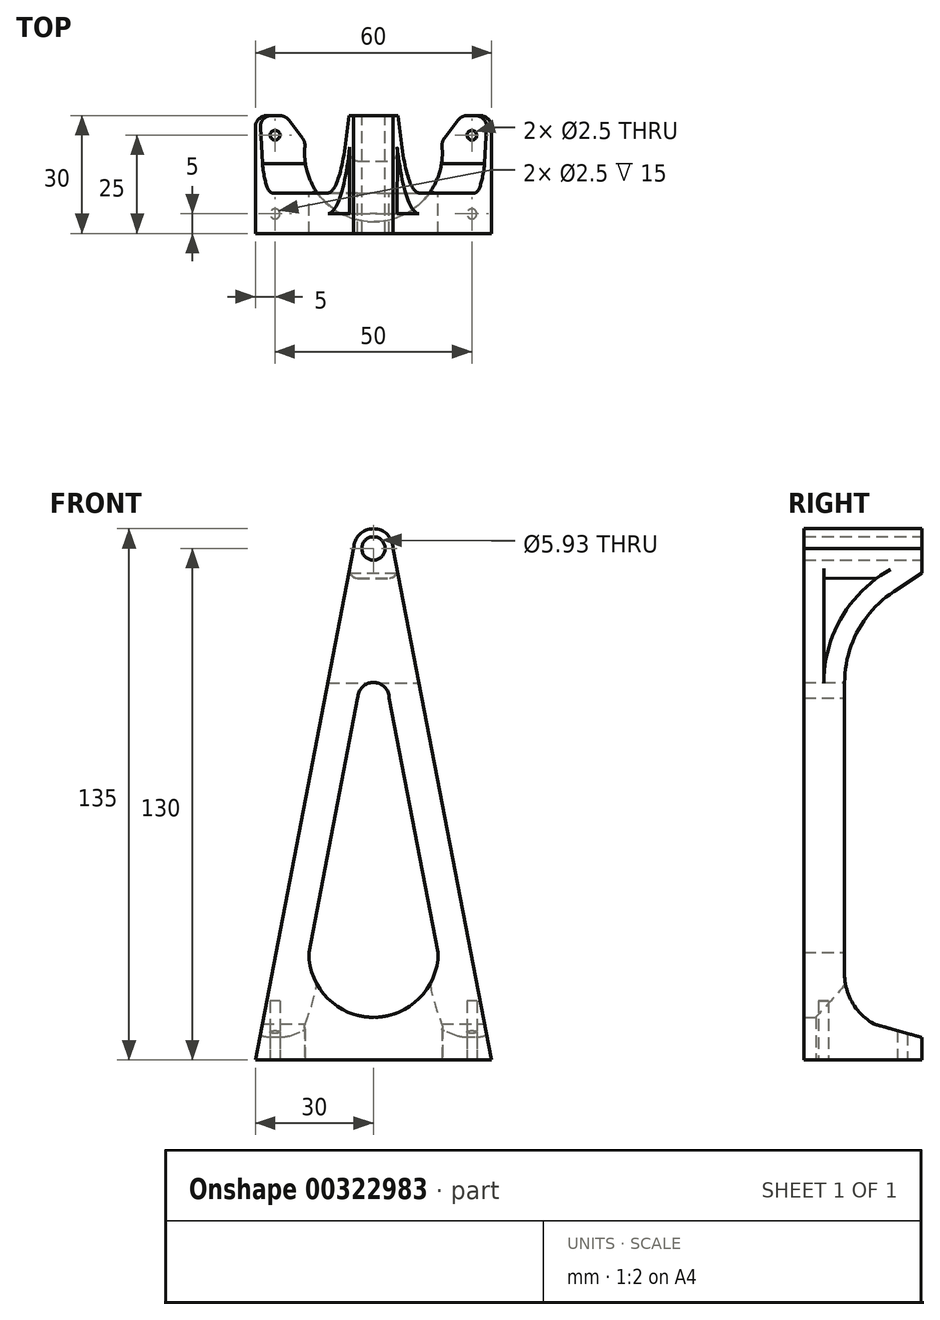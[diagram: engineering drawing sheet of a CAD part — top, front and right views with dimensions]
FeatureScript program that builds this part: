
annotation { "Feature Type Name" : "Feature", "Feature Type Description" : "" }
export const myFeature = defineFeature(function(context is Context, id is Id, definition is map)
    precondition{}
    {
        {
            var Q0;
            Q0=qCreatedBy(makeId("Front.planeOp"),FACE);
            var sketch = newSketch(context, id + "F0", { "sketchPlane" : qUnion([Q0])});
            skLineSegment(sketch, "E0", {"start": v(0, 0) * mm, "end": v(0, 130) * mm, "construction": true});
            skLineSegment(sketch, "E1", {"start": v(0, 130) * mm, "end": v(-5, 130) * mm, "construction": true});
            skLineSegment(sketch, "E2", {"start": v(0, 0) * mm, "end": v(-30, 0) * mm});
            skLineSegment(sketch, "E3", {"start": v(-30, 0) * mm, "end": v(-5, 130) * mm});
            skLineSegment(sketch, "E4.MirrorCS", {"start": v(30, 0) * mm, "end": v(5, 130) * mm});
            skLineSegment(sketch, "E5.MirrorCS", {"start": v(0, 0) * mm, "end": v(30, 0) * mm});
            skArc(sketch, "E6", {"start": v(-5, 130) * mm, "mid": v(0, 135) * mm, "end": v(5, 130) * mm});
            skCircle(sketch, "E7", {"center": v(0, 27.3) * mm, "radius": 16.43 * mm, "construction": true});
            skCircle(sketch, "E8", {"center": v(0, 130) * mm, "radius": 5 * mm, "construction": true});
            skCircle(sketch, "E9", {"center": v(0, 115.44) * mm, "radius": 0.58 * mm, "construction": true});
            skLineSegment(sketch, "E10", {"start": v(-0.31, 115.93) * mm, "end": v(16.13, 30.4) * mm, "construction": true});
            skLineSegment(sketch, "E11.MirrorCS", {"start": v(0.31, 115.93) * mm, "end": v(-16.13, 30.4) * mm, "construction": true});
            skCircle(sketch, "E12", {"center": v(0, 91.94) * mm, "radius": 4.22 * mm, "construction": true});
            skLineSegment(sketch, "E13", {"start": v(0, 91.94) * mm, "end": v(-10.67, 91.94) * mm, "construction": true});
            skLineSegment(sketch, "E14", {"start": v(0, 91.94) * mm, "end": v(7.84, 91.94) * mm, "construction": true});
            skLineSegment(sketch, "E15", {"start": v(0, 27.3) * mm, "end": v(21.13, 27.3) * mm, "construction": true});
            skLineSegment(sketch, "E16", {"start": v(0, 27.3) * mm, "end": v(-22.3, 27.3) * mm, "construction": true});
            skLineSegment(sketch, "E17", {"start": v(-16.43, 27.3) * mm, "end": v(-4, 91.94) * mm});
            skLineSegment(sketch, "E18.MirrorCS", {"start": v(16.43, 27.3) * mm, "end": v(4, 91.94) * mm});
            skArc(sketch, "E19", {"start": v(-4, 91.94) * mm, "mid": v(0, 95.94) * mm, "end": v(4, 91.94) * mm});
            skArc(sketch, "E20", {"start": v(-16.43, 27.3) * mm, "mid": v(0, 10.87) * mm, "end": v(16.43, 27.3) * mm});
            skCircle(sketch, "E21", {"center": v(0, 130) * mm, "radius": 2.97 * mm});
            skSolve(sketch);
        }
        {
            var Q0;
            Q0 = qSketchRegion(id + "F0", true);
            extrude(context, id + "F1", {"entities" : qUnion([Q0]), "depth" : 30 * mm, "symmetric" : true});
        }
        {
            var Q0;
            Q0=qCreatedBy(makeId("Top.planeOp"),FACE);
            var sketch = newSketch(context, id + "F2", { "sketchPlane" : qUnion([Q0])});
            skLineSegment(sketch, "E22.bottom", {"start": v(31.25, -15.95) * mm, "end": v(-31.25, -15.95) * mm, "construction": true});
            skLineSegment(sketch, "E22.top", {"start": v(31.25, 15.95) * mm, "end": v(-31.25, 15.95) * mm, "construction": true});
            skLineSegment(sketch, "E22.left", {"start": v(31.25, -15.95) * mm, "end": v(31.25, 15.95) * mm, "construction": true});
            skLineSegment(sketch, "E22.right", {"start": v(-31.25, -15.95) * mm, "end": v(-31.25, 15.95) * mm, "construction": true});
            skPoint(sketch, "E22.middle", {"position": v(0, 0) * mm});
            skLineSegment(sketch, "E23.bottom", {"start": v(25, -10) * mm, "end": v(-25, -10) * mm, "construction": true});
            skLineSegment(sketch, "E23.top", {"start": v(25, 10) * mm, "end": v(-25, 10) * mm, "construction": true});
            skLineSegment(sketch, "E23.left", {"start": v(25, -10) * mm, "end": v(25, 10) * mm, "construction": true});
            skLineSegment(sketch, "E23.right", {"start": v(-25, -10) * mm, "end": v(-25, 10) * mm, "construction": true});
            skCircle(sketch, "E24", {"center": v(-25, -10) * mm, "radius": 1.25 * mm});
            skLineSegment(sketch, "E25", {"start": v(-25, 10) * mm, "end": v(25, 10) * mm});
            skCircle(sketch, "E26", {"center": v(-25, 10) * mm, "radius": 1.25 * mm});
            skCircle(sketch, "E27", {"center": v(25, 10) * mm, "radius": 1.25 * mm});
            skCircle(sketch, "E28", {"center": v(25, -10) * mm, "radius": 1.25 * mm});
            skSolve(sketch);
        }
        {
            var Q0;
            Q0 = qSketchRegion(id + "F2", true);
            extrude(context, id + "F3", {"entities" : qUnion([Q0]), "operationType" : NewBodyOperationType.REMOVE, "depth" : 15 * mm});
        }
        {
            var Q0;
            Q0=qCreatedBy(makeId("Right.planeOp"),FACE);
            var sketch = newSketch(context, id + "F4", { "sketchPlane" : qUnion([Q0])});
            skLineSegment(sketch, "E29", {"start": v(17.72, 4.98) * mm, "end": v(2.8, 9.16) * mm});
            skLineSegment(sketch, "E30", {"start": v(-4.67, 22) * mm, "end": v(-4.67, 95.84) * mm});
            skLineSegment(sketch, "E31", {"start": v(7.82, 119) * mm, "end": v(19.16, 126.47) * mm});
            skArc(sketch, "E32", {"start": v(7.82, 119) * mm, "mid": v(-1.35, 109) * mm, "end": v(-4.67, 95.84) * mm});
            skArc(sketch, "E33", {"start": v(-4.67, 22) * mm, "mid": v(-2.67, 14.57) * mm, "end": v(2.8, 9.16) * mm});
            skLineSegment(sketch, "E34", {"start": v(19.16, 126.47) * mm, "end": v(17.72, 4.98) * mm});
            skArc(sketch, "E35.0", {"start": v(3.86, 122.35) * mm, "mid": v(-6.42, 110.06) * mm, "end": v(-9.64, 94.37) * mm});
            skArc(sketch, "E36.0", {"start": v(3.7, 122.57) * mm, "mid": v(-6.67, 110.18) * mm, "end": v(-9.92, 94.36) * mm});
            skLineSegment(sketch, "E37", {"start": v(3.86, 122.35) * mm, "end": v(-9.95, 122.5) * mm});
            skLineSegment(sketch, "E38", {"start": v(-9.95, 122.5) * mm, "end": v(-9.95, 94.33) * mm});
            skSolve(sketch);
        }
        {
            var Q0;
            Q0 = qSketchRegion(id + "F4", true);
            extrude(context, id + "F5", {"entities" : qUnion([Q0]), "operationType" : NewBodyOperationType.REMOVE, "oppositeDirection" : true, "depth" : 60 * mm, "symmetric" : true});
        }
        {
            var Q0;
            Q0=qCreatedBy(makeId("Top.planeOp"),FACE);
            var sketch = newSketch(context, id + "F6", { "sketchPlane" : qUnion([Q0])});
            skCircle(sketch, "E39", {"center": v(0, 0) * mm, "radius": 8.81 * mm});
            skLineSegment(sketch, "E40", {"start": v(-7.03, -5.32) * mm, "end": v(-22.8, 15.52) * mm});
            skLineSegment(sketch, "E41", {"start": v(-22.8, 15.52) * mm, "end": v(0, 15.52) * mm});
            skLineSegment(sketch, "E42.MirrorCS", {"start": v(7.03, -5.32) * mm, "end": v(22.8, 15.52) * mm});
            skLineSegment(sketch, "E43.MirrorCS", {"start": v(22.8, 15.52) * mm, "end": v(0, 15.52) * mm});
            skSolve(sketch);
        }
        {
            var Q0;
            Q0 = qSketchRegion(id + "F6", true);
            extrude(context, id + "F7", {"entities" : qUnion([Q0]), "operationType" : NewBodyOperationType.REMOVE, "depth" : 25 * mm});
        }
        {
            var Q0;
            {var subQ0=sQuery(id+"F0.wireOp",EDGE,"E5.MirrorCS");var subQ1=sQuery(id+"F0.wireOp",EDGE,"E2");var subQ2=sQuery(id+"F0.wireOp",EDGE,"E3");var subQ3=sQuery(id+"F0.wireOp",EDGE,"E4.MirrorCS");Q0=makeQuery(id+"F7.boolean.opBoolean","INTERSECT",EDGE,{"derivedFrom":[makeQuery(id+"F5.boolean.opBoolean","SPLIT",FACE,{"disambiguationData":[TD([makeQuery(id+"F5.opExtrude","SWEPT_FACE",FACE,{"disambiguationData":[OSD([sQuery(id+"F4.wireOp",EDGE,"E29")])]})])],"derivedFrom":makeQuery(id+"F1.opExtrude","CAP_FACE",FACE,{"disambiguationData":[OSD([subQ1,subQ2,subQ3,subQ0,sQuery(id+"F0.wireOp",EDGE,"E6"),sQuery(id+"F0.wireOp",EDGE,"E17"),sQuery(id+"F0.wireOp",EDGE,"E18.MirrorCS"),sQuery(id+"F0.wireOp",EDGE,"E19"),sQuery(id+"F0.wireOp",EDGE,"E20"),sQuery(id+"F0.wireOp",EDGE,"E21")])],"isStart":true})}),makeQuery(id+"F7.opExtrude","SWEPT_FACE",FACE,{"disambiguationData":[OSD([sQuery(id+"F6.wireOp",EDGE,"E42.MirrorCS")])]})]});}
            fillet(context, id + "F8", {"entities" : qUnion([Q0]), "radius" : 3 * mm, "tangentPropagation" : true, "allowEdgeOverflow" : false});
        }
        {
            var Q0;
            {var subQ0=sQuery(id+"F0.wireOp",EDGE,"E5.MirrorCS");var subQ1=sQuery(id+"F0.wireOp",EDGE,"E2");var subQ2=sQuery(id+"F0.wireOp",EDGE,"E3");var subQ3=sQuery(id+"F0.wireOp",EDGE,"E4.MirrorCS");Q0=makeQuery(id+"F7.boolean.opBoolean","INTERSECT",EDGE,{"derivedFrom":[makeQuery(id+"F5.boolean.opBoolean","SPLIT",FACE,{"disambiguationData":[TD([makeQuery(id+"F5.opExtrude","SWEPT_FACE",FACE,{"disambiguationData":[OSD([sQuery(id+"F4.wireOp",EDGE,"E29")])]})])],"derivedFrom":makeQuery(id+"F1.opExtrude","CAP_FACE",FACE,{"disambiguationData":[OSD([subQ1,subQ2,subQ3,subQ0,sQuery(id+"F0.wireOp",EDGE,"E6"),sQuery(id+"F0.wireOp",EDGE,"E17"),sQuery(id+"F0.wireOp",EDGE,"E18.MirrorCS"),sQuery(id+"F0.wireOp",EDGE,"E19"),sQuery(id+"F0.wireOp",EDGE,"E20"),sQuery(id+"F0.wireOp",EDGE,"E21")])],"isStart":true})}),makeQuery(id+"F7.opExtrude","SWEPT_FACE",FACE,{"disambiguationData":[OSD([sQuery(id+"F6.wireOp",EDGE,"E40")])]})]});}
            var Q1;
            {var subQ1=sQuery(id+"F0.wireOp",EDGE,"E3");Q1=makeQuery(id+"F5.boolean.opBoolean","SPLIT",EDGE,{"disambiguationData":[TD([makeQuery(id+"F5.opExtrude","SWEPT_FACE",FACE,{"disambiguationData":[OSD([sQuery(id+"F4.wireOp",EDGE,"E29")])]})])],"derivedFrom":makeQuery(id+"F1.opExtrude","CAP_EDGE",EDGE,{"disambiguationData":[OSD([subQ1])],"isStart":true})});}
            var Q2;
            {var subQ1=sQuery(id+"F0.wireOp",EDGE,"E4.MirrorCS");Q2=makeQuery(id+"F5.boolean.opBoolean","SPLIT",EDGE,{"disambiguationData":[TD([makeQuery(id+"F5.opExtrude","SWEPT_FACE",FACE,{"disambiguationData":[OSD([sQuery(id+"F4.wireOp",EDGE,"E29")])]})])],"derivedFrom":makeQuery(id+"F1.opExtrude","CAP_EDGE",EDGE,{"disambiguationData":[OSD([subQ1])],"isStart":true})});}
            fillet(context, id + "F9", {"entities" : qUnion([Q0, Q1, Q2]), "radius" : 3 * mm, "tangentPropagation" : true, "allowEdgeOverflow" : false});
        }
        {
            var Q0;
            Q0=qCreatedBy(makeId("Top.planeOp"),FACE);
            var sketch = newSketch(context, id + "F10", { "sketchPlane" : qUnion([Q0])});
            skCircle(sketch, "E44", {"center": v(0, 5.5) * mm, "radius": 17.5 * mm});
            skSolve(sketch);
        }
        {
            var Q0;
            Q0 = qSketchRegion(id + "F10", true);
            extrude(context, id + "F11", {"entities" : qUnion([Q0]), "operationType" : NewBodyOperationType.REMOVE, "depth" : 30 * mm});
        }
        {
            var Q0;
            Q0=makeQuery(id+"F11.boolean.opBoolean","INTERSECT",EDGE,{"derivedFrom":[makeQuery(id+"F7.boolean.opBoolean","COPY",FACE,{"derivedFrom":makeQuery(id+"F7.opExtrude","SWEPT_FACE",FACE,{"disambiguationData":[OSD([sQuery(id+"F6.wireOp",EDGE,"E40")])]})}),makeQuery(id+"F11.opExtrude","SWEPT_FACE",FACE,{"disambiguationData":[OSD([sQuery(id+"F10.wireOp",EDGE,"E44")])]})]});
            var Q1;
            Q1=makeQuery(id+"F11.boolean.opBoolean","INTERSECT",EDGE,{"derivedFrom":[makeQuery(id+"F7.boolean.opBoolean","COPY",FACE,{"derivedFrom":makeQuery(id+"F7.opExtrude","SWEPT_FACE",FACE,{"disambiguationData":[OSD([sQuery(id+"F6.wireOp",EDGE,"E42.MirrorCS")])]})}),makeQuery(id+"F11.opExtrude","SWEPT_FACE",FACE,{"disambiguationData":[OSD([sQuery(id+"F10.wireOp",EDGE,"E44")])]})]});
            fillet(context, id + "F12", {"entities" : qUnion([Q0, Q1]), "radius" : 3 * mm, "tangentPropagation" : true, "allowEdgeOverflow" : false});
        }
        {
            var Q0;
            Q0=makeQuery(id+"F5.boolean.opBoolean","INTERSECT",EDGE,{"derivedFrom":[makeQuery(id+"F1.opExtrude","SWEPT_FACE",FACE,{"disambiguationData":[OSD([sQuery(id+"F0.wireOp",EDGE,"E3")])]}),makeQuery(id+"F5.opExtrude","SWEPT_FACE",FACE,{"disambiguationData":[OSD([sQuery(id+"F4.wireOp",EDGE,"E37")])]})]});
            var Q1;
            Q1=makeQuery(id+"F5.boolean.opBoolean","INTERSECT",EDGE,{"derivedFrom":[makeQuery(id+"F1.opExtrude","SWEPT_FACE",FACE,{"disambiguationData":[OSD([sQuery(id+"F0.wireOp",EDGE,"E4.MirrorCS")])]}),makeQuery(id+"F5.opExtrude","SWEPT_FACE",FACE,{"disambiguationData":[OSD([sQuery(id+"F4.wireOp",EDGE,"E37")])]})]});
            fillet(context, id + "F13", {"entities" : qUnion([Q0, Q1]), "radius" : 2 * mm, "tangentPropagation" : true, "allowEdgeOverflow" : false});
        }
    });
